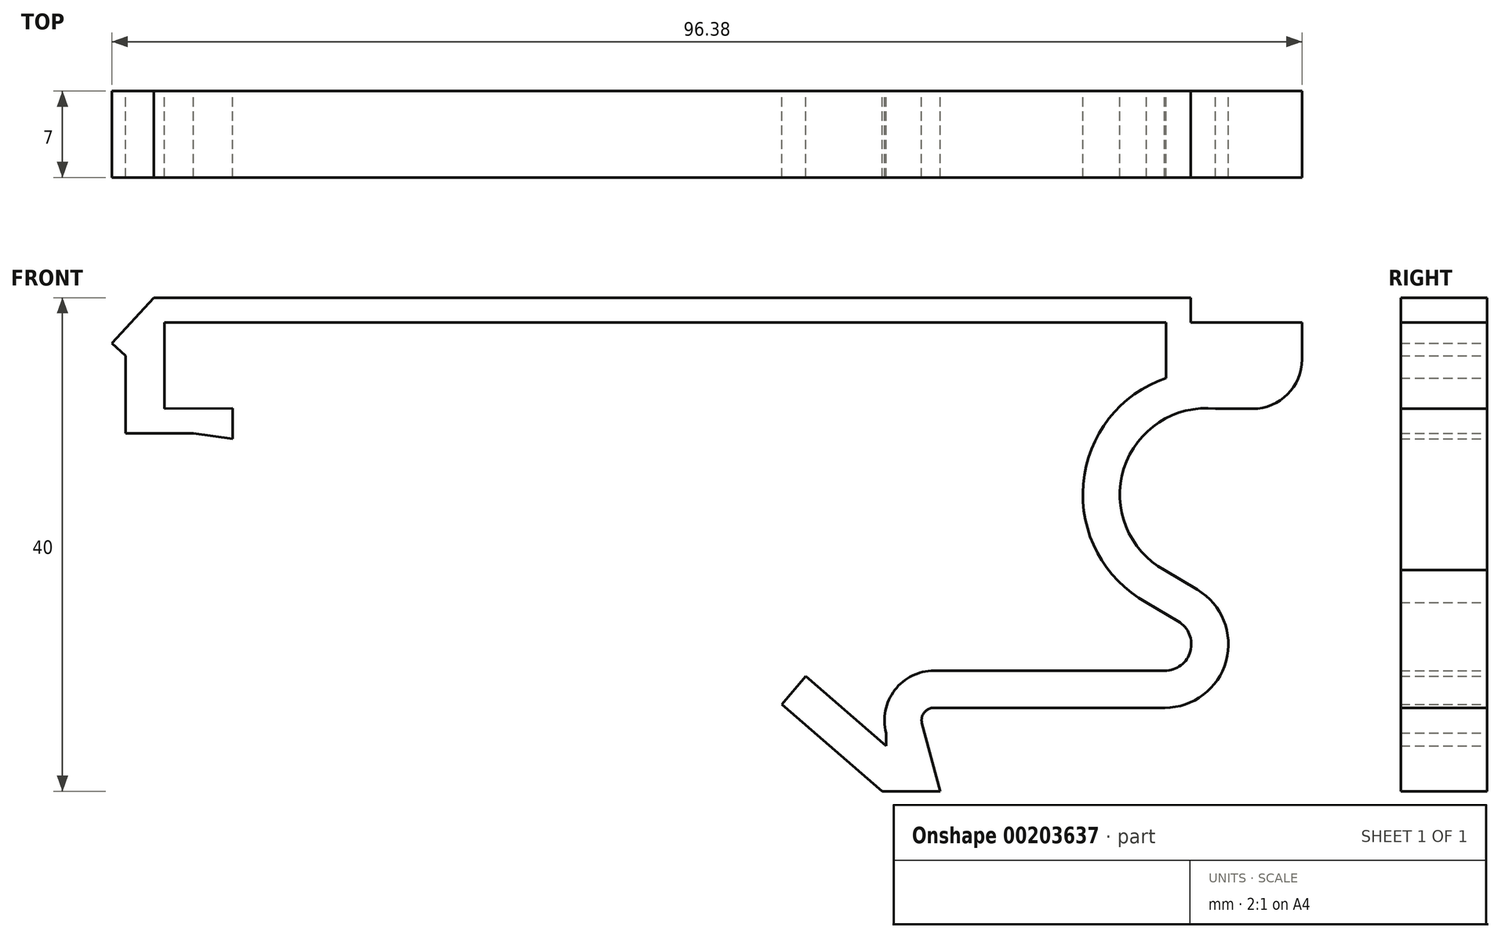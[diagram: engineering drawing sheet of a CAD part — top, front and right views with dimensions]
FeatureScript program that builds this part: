
annotation { "Feature Type Name" : "Feature", "Feature Type Description" : "" }
export const myFeature = defineFeature(function(context is Context, id is Id, definition is map)
    precondition{}
    {
        {
            var Q0;
            Q0=qCreatedBy(makeId("Front.planeOp"),FACE);
            var sketch = newSketch(context, id + "F0", { "sketchPlane" : qUnion([Q0])});
            skLineSegment(sketch, "E0", {"start": v(0, 0) * mm, "end": v(-84, 0) * mm});
            skLineSegment(sketch, "E1", {"start": v(-84, 0) * mm, "end": v(-87.38, -3.69) * mm});
            skLineSegment(sketch, "E2", {"start": v(-87.38, -3.69) * mm, "end": v(-86.27, -4.7) * mm});
            skLineSegment(sketch, "E3", {"start": v(-86.27, -4.7) * mm, "end": v(-86.27, -11) * mm});
            skLineSegment(sketch, "E4", {"start": v(-86.27, -11) * mm, "end": v(-80.77, -11) * mm});
            skLineSegment(sketch, "E5", {"start": v(-80.77, -11) * mm, "end": v(-77.6, -11.42) * mm});
            skLineSegment(sketch, "E6", {"start": v(-33.14, -32.96) * mm, "end": v(-25, -40) * mm});
            skLineSegment(sketch, "E7", {"start": v(-25, -40) * mm, "end": v(-20.3, -40) * mm});
            skLineSegment(sketch, "E8", {"start": v(-20.3, -40) * mm, "end": v(-21.77, -34.5) * mm});
            skLineSegment(sketch, "E9", {"start": v(-20.8, -33.24) * mm, "end": v(-2.11, -33.24) * mm});
            skLineSegment(sketch, "E10", {"start": v(0, 0) * mm, "end": v(0, -2) * mm});
            skLineSegment(sketch, "E11", {"start": v(0, -2) * mm, "end": v(9, -2) * mm});
            skLineSegment(sketch, "E12", {"start": v(9, -2) * mm, "end": v(9, -5) * mm});
            skLineSegment(sketch, "E13", {"start": v(5, -9) * mm, "end": v(2, -9) * mm});
            skArc(sketch, "E14", {"start": v(-2.11, -33.24) * mm, "mid": v(2.86, -29.44) * mm, "end": v(0.5, -23.65) * mm});
            skArc(sketch, "E15", {"start": v(2, -9) * mm, "mid": v(-5.42, -13.85) * mm, "end": v(-2.13, -22.09) * mm});
            skLineSegment(sketch, "E16", {"start": v(0.54, -23.67) * mm, "end": v(-2.5, -21.87) * mm});
            skPoint(sketch, "E17.visualSharp", {"position": v(-22.11, -33.24) * mm});
            skArc(sketch, "E17.filletArc", {"start": v(-20.8, -33.24) * mm, "mid": v(-21.6, -33.63) * mm, "end": v(-21.77, -34.5) * mm});
            skPoint(sketch, "E18.visualSharp", {"position": v(9, -9) * mm});
            skArc(sketch, "E18.filletArc", {"start": v(5, -9) * mm, "mid": v(7.83, -7.83) * mm, "end": v(9, -5) * mm});
            skLineSegment(sketch, "E19.0", {"start": v(-2, -2) * mm, "end": v(-83.12, -2) * mm});
            skLineSegment(sketch, "E20.1", {"start": v(-83.12, -9) * mm, "end": v(-77.62, -8.95) * mm});
            skLineSegment(sketch, "E21", {"start": v(-83.12, -2) * mm, "end": v(-83.12, -9) * mm});
            skLineSegment(sketch, "E22", {"start": v(-77.62, -8.95) * mm, "end": v(-77.6, -11.42) * mm});
            skArc(sketch, "E23.0", {"start": v(-2, -6.5) * mm, "mid": v(-8.71, -15.1) * mm, "end": v(-3.59, -24.71) * mm});
            skArc(sketch, "E24.0", {"start": v(-2.11, -30.24) * mm, "mid": v(-0.04, -28.65) * mm, "end": v(-1.02, -26.23) * mm});
            skLineSegment(sketch, "E25", {"start": v(-1.02, -26.23) * mm, "end": v(-3.59, -24.71) * mm});
            skLineSegment(sketch, "E26", {"start": v(-2, -2) * mm, "end": v(-2, -6.5) * mm});
            skLineSegment(sketch, "E27.0", {"start": v(-20.8, -30.24) * mm, "end": v(-2.11, -30.24) * mm});
            skLineSegment(sketch, "E28.0", {"start": v(-31.18, -30.7) * mm, "end": v(-24.67, -36.32) * mm});
            skArc(sketch, "E29.0", {"start": v(-20.8, -30.24) * mm, "mid": v(-23.98, -31.8) * mm, "end": v(-24.67, -35.27) * mm});
            skLineSegment(sketch, "E30", {"start": v(-24.67, -35.27) * mm, "end": v(-24.67, -36.32) * mm});
            skLineSegment(sketch, "E31", {"start": v(-31.18, -30.7) * mm, "end": v(-33.14, -32.96) * mm});
            skSolve(sketch);
        }
        {
            var Q0;
            {var subQ0=sQuery(id+"F0.wireOp",EDGE,"E16");var subQ1=sQuery(id+"F0.wireOp",EDGE,"E14");var subQ2=makeQuery(id+"F0.imprint","INTERSECT",VERTEX,{"disambiguationData":[OD(0.0)],"derivedFrom":[subQ1,subQ0]});Q0=makeQuery(id+"F0.imprint","IMPRINT",FACE,{"disambiguationData":[TD([[makeQuery(id+"F0.imprint","IMPRINT",EDGE,{"disambiguationData":[TD([[subQ2,-1.0]])],"derivedFrom":subQ1}),1.0]])]});}
            var Q1;
            {var subQ0=sQuery(id+"F0.wireOp",EDGE,"E14");var subQ1=makeQuery(id+"F0.imprint","INTERSECT",VERTEX,{"derivedFrom":[sQuery(id+"F0.wireOp",EDGE,"E9"),subQ0]});Q1=makeQuery(id+"F0.imprint","IMPRINT",FACE,{"disambiguationData":[TD([[makeQuery(id+"F0.imprint","IMPRINT",EDGE,{"disambiguationData":[TD([[subQ1,1.0]])],"derivedFrom":subQ0}),1.0]])]});}
            var Q2;
            {var subQ0=sQuery(id+"F0.wireOp",EDGE,"E16");var subQ1=sQuery(id+"F0.wireOp",EDGE,"E15");var subQ2=makeQuery(id+"F0.imprint","INTERSECT",VERTEX,{"disambiguationData":[OD(0.0)],"derivedFrom":[subQ1,subQ0]});Q2=makeQuery(id+"F0.imprint","IMPRINT",FACE,{"disambiguationData":[TD([[makeQuery(id+"F0.imprint","IMPRINT",EDGE,{"disambiguationData":[TD([[subQ2,-1.0]])],"derivedFrom":subQ1}),1.0]])]});}
            var Q3;
            Q3=makeQuery(id+"F0.imprint","IMPRINT",FACE,{"disambiguationData":[TD([[makeQuery(id+"F0.imprint","IMPRINT",EDGE,{"derivedFrom":sQuery(id+"F0.wireOp",EDGE,"E0")}),1.0]])]});
            extrude(context, id + "F1", {"entities" : qUnion([Q0, Q1, Q2, Q3]), "depth" : 7 * mm});
        }
    });
